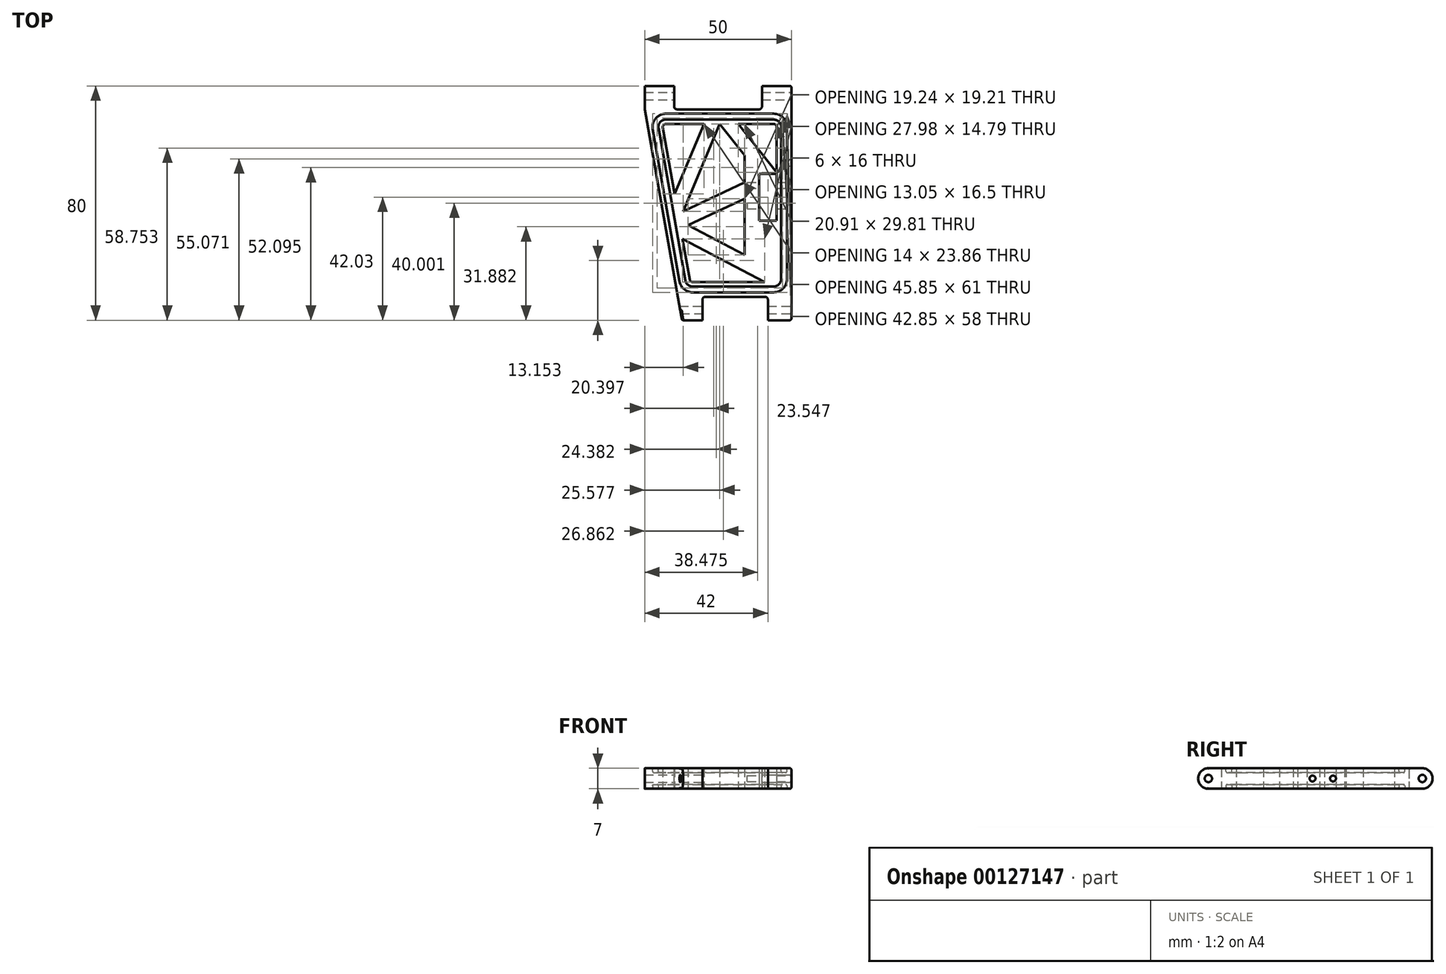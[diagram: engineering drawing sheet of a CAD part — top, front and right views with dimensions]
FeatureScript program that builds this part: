
annotation { "Feature Type Name" : "Feature", "Feature Type Description" : "" }
export const myFeature = defineFeature(function(context is Context, id is Id, definition is map)
    precondition{}
    {
        {
            var Q0;
            Q0=qCreatedBy(makeId("Top.planeOp"),FACE);
            var sketch = newSketch(context, id + "F0", { "sketchPlane" : qUnion([Q0])});
            skLineSegment(sketch, "E0", {"start": v(-39, 45.97) * mm, "end": v(-39, 37.97) * mm});
            skLineSegment(sketch, "E1", {"start": v(-39, 37.97) * mm, "end": v(-26.3, -34.03) * mm});
            skLineSegment(sketch, "E2", {"start": v(11, -34.03) * mm, "end": v(11, 45.97) * mm});
            skLineSegment(sketch, "E3", {"start": v(11, 45.97) * mm, "end": v(1, 45.97) * mm});
            skLineSegment(sketch, "E4", {"start": v(1, 45.97) * mm, "end": v(1, 38.97) * mm});
            skLineSegment(sketch, "E5", {"start": v(-39, 45.97) * mm, "end": v(-29, 45.97) * mm});
            skLineSegment(sketch, "E6", {"start": v(-29, 45.97) * mm, "end": v(-29, 38.97) * mm});
            skLineSegment(sketch, "E7", {"start": v(-28, 37.97) * mm, "end": v(0, 37.97) * mm});
            skLineSegment(sketch, "E8", {"start": v(-26.3, -34.03) * mm, "end": v(-19.3, -34.03) * mm});
            skLineSegment(sketch, "E9", {"start": v(-19.3, -34.03) * mm, "end": v(-19.3, -27.03) * mm});
            skLineSegment(sketch, "E10", {"start": v(11, -34.03) * mm, "end": v(3, -34.03) * mm});
            skLineSegment(sketch, "E11", {"start": v(3, -34.03) * mm, "end": v(3, -27.03) * mm});
            skLineSegment(sketch, "E12", {"start": v(2, -26.03) * mm, "end": v(-18.3, -26.03) * mm});
            skPoint(sketch, "E13.visualSharp", {"position": v(-29, 37.97) * mm});
            skArc(sketch, "E13.filletArc", {"start": v(-29, 38.97) * mm, "mid": v(-28.7, 38.26) * mm, "end": v(-28, 37.97) * mm});
            skPoint(sketch, "E14.visualSharp", {"position": v(1, 37.97) * mm});
            skArc(sketch, "E14.filletArc", {"start": v(0, 37.97) * mm, "mid": v(0.7, 38.26) * mm, "end": v(1, 38.97) * mm});
            skPoint(sketch, "E15.visualSharp", {"position": v(-19.3, -26.03) * mm});
            skArc(sketch, "E15.filletArc", {"start": v(-18.3, -26.03) * mm, "mid": v(-19.01, -26.32) * mm, "end": v(-19.3, -27.03) * mm});
            skPoint(sketch, "E16.visualSharp", {"position": v(3, -26.03) * mm});
            skArc(sketch, "E16.filletArc", {"start": v(3, -27.03) * mm, "mid": v(2.7, -26.32) * mm, "end": v(2, -26.03) * mm});
            skLineSegment(sketch, "E17", {"start": v(6, -20.03) * mm, "end": v(6, 31.97) * mm});
            skLineSegment(sketch, "E18", {"start": v(5, 32.97) * mm, "end": v(-31.85, 32.97) * mm});
            skLineSegment(sketch, "E19", {"start": v(-32.83, 31.8) * mm, "end": v(-23.67, -20.2) * mm});
            skLineSegment(sketch, "E20", {"start": v(-22.68, -21.03) * mm, "end": v(5, -21.03) * mm});
            skPoint(sketch, "E21.visualSharp", {"position": v(-33.04, 32.97) * mm});
            skArc(sketch, "E21.filletArc", {"start": v(-31.85, 32.97) * mm, "mid": v(-32.62, 32.61) * mm, "end": v(-32.83, 31.8) * mm});
            skPoint(sketch, "E22.visualSharp", {"position": v(6, 32.97) * mm});
            skArc(sketch, "E22.filletArc", {"start": v(6, 31.97) * mm, "mid": v(5.7, 32.68) * mm, "end": v(5, 32.97) * mm});
            skPoint(sketch, "E23.visualSharp", {"position": v(-23.52, -21.03) * mm});
            skArc(sketch, "E23.filletArc", {"start": v(-23.67, -20.2) * mm, "mid": v(-23.32, -20.8) * mm, "end": v(-22.68, -21.03) * mm});
            skPoint(sketch, "E24.visualSharp", {"position": v(6, -21.03) * mm});
            skArc(sketch, "E24.filletArc", {"start": v(5, -21.03) * mm, "mid": v(5.7, -20.74) * mm, "end": v(6, -20.03) * mm});
            skLineSegment(sketch, "E25", {"start": v(0, 0) * mm, "end": v(0, 16) * mm});
            skLineSegment(sketch, "E26", {"start": v(0, 16) * mm, "end": v(6, 16) * mm});
            skLineSegment(sketch, "E27", {"start": v(0, 0) * mm, "end": v(6, 0) * mm});
            skLineSegment(sketch, "E28", {"start": v(-13.42, 32.97) * mm, "end": v(0, 16) * mm});
            skLineSegment(sketch, "E29", {"start": v(-7.05, 32.97) * mm, "end": v(6, 16.47) * mm});
            skPoint(sketch, "E29.startSnap0", {"position": v(-6.71, 24.49) * mm});
            skPoint(sketch, "E29.endSnap0", {"position": v(3, 16) * mm});
            skLineSegment(sketch, "E30", {"start": v(-13.42, 32.97) * mm, "end": v(-13.42, -21.03) * mm, "construction": true});
            skLineSegment(sketch, "E31", {"start": v(-13.42, 32.97) * mm, "end": v(-27.23, 0) * mm});
            skLineSegment(sketch, "E32", {"start": v(-18.74, 33.22) * mm, "end": v(-28.83, 9.11) * mm});
            skLineSegment(sketch, "E33", {"start": v(-27.23, 0) * mm, "end": v(6, -17.57) * mm});
            skLineSegment(sketch, "E34", {"start": v(-26.13, -6.24) * mm, "end": v(1.85, -21.03) * mm});
            skLineSegment(sketch, "E35", {"start": v(-5, 22.32) * mm, "end": v(-5, -11.75) * mm});
            skLineSegment(sketch, "E36", {"start": v(-25.9, 3.16) * mm, "end": v(-5, 12.98) * mm});
            skLineSegment(sketch, "E37", {"start": v(-24.24, -1.58) * mm, "end": v(-5, 7.45) * mm});
            skArc(sketch, "E38.0", {"start": v(7.5, 31.97) * mm, "mid": v(6.77, 33.74) * mm, "end": v(5, 34.47) * mm});
            skLineSegment(sketch, "E38.1", {"start": v(7.5, -20.03) * mm, "end": v(7.5, 31.97) * mm});
            skLineSegment(sketch, "E38.2", {"start": v(5, 34.47) * mm, "end": v(-31.85, 34.47) * mm});
            skArc(sketch, "E38.3", {"start": v(5, -22.53) * mm, "mid": v(6.77, -21.8) * mm, "end": v(7.5, -20.03) * mm});
            skArc(sketch, "E38.4", {"start": v(-31.85, 34.47) * mm, "mid": v(-33.76, 33.58) * mm, "end": v(-34.31, 31.54) * mm});
            skLineSegment(sketch, "E38.5", {"start": v(-34.31, 31.54) * mm, "end": v(-25.14, -20.46) * mm});
            skArc(sketch, "E38.6", {"start": v(-25.14, -20.46) * mm, "mid": v(-24.29, -21.94) * mm, "end": v(-22.68, -22.53) * mm});
            skLineSegment(sketch, "E38.7", {"start": v(-22.68, -22.53) * mm, "end": v(5, -22.53) * mm});
            skArc(sketch, "E39.0", {"start": v(9.5, 31.97) * mm, "mid": v(8.18, 35.15) * mm, "end": v(5, 36.47) * mm});
            skLineSegment(sketch, "E39.1", {"start": v(9.5, -20.03) * mm, "end": v(9.5, 31.97) * mm});
            skLineSegment(sketch, "E39.2", {"start": v(5, 36.47) * mm, "end": v(-31.85, 36.47) * mm});
            skArc(sketch, "E39.3", {"start": v(5, -24.53) * mm, "mid": v(8.18, -23.21) * mm, "end": v(9.5, -20.03) * mm});
            skArc(sketch, "E39.4", {"start": v(-31.85, 36.47) * mm, "mid": v(-35.3, 34.86) * mm, "end": v(-36.28, 31.19) * mm});
            skLineSegment(sketch, "E39.5", {"start": v(-36.28, 31.19) * mm, "end": v(-27.11, -20.81) * mm});
            skArc(sketch, "E39.6", {"start": v(-27.11, -20.81) * mm, "mid": v(-25.57, -23.48) * mm, "end": v(-22.68, -24.53) * mm});
            skLineSegment(sketch, "E39.7", {"start": v(-22.68, -24.53) * mm, "end": v(5, -24.53) * mm});
            skSolve(sketch);
        }
        {
            var Q0;
            Q0=makeQuery(id+"F0.imprint","IMPRINT",FACE,{"disambiguationData":[TD([[makeQuery(id+"F0.imprint","IMPRINT",EDGE,{"derivedFrom":sQuery(id+"F0.wireOp",EDGE,"E0")}),1.0]])]});
            var Q1;
            Q1=makeQuery(id+"F0.imprint","IMPRINT",FACE,{"disambiguationData":[TD([[makeQuery(id+"F0.imprint","IMPRINT",EDGE,{"derivedFrom":sQuery(id+"F0.wireOp",EDGE,"E38.0")}),-1.0]])]});
            var Q2;
            {var subQ22=sQuery(id+"F0.wireOp",EDGE,"E21.filletArc");Q2=makeQuery(id+"F0.imprint","IMPRINT",FACE,{"disambiguationData":[TD([[makeQuery(id+"F0.imprint","IMPRINT",EDGE,{"derivedFrom":subQ22}),-1.0]])]});}
            var Q3;
            {var subQ0=sQuery(id+"F0.wireOp",EDGE,"E24.filletArc");Q3=makeQuery(id+"F0.imprint","IMPRINT",FACE,{"disambiguationData":[TD([[makeQuery(id+"F0.imprint","IMPRINT",EDGE,{"derivedFrom":subQ0}),1.0]])]});}
            var Q4;
            {var subQ0=sQuery(id+"F0.wireOp",EDGE,"E36");Q4=makeQuery(id+"F0.imprint","IMPRINT",FACE,{"disambiguationData":[TD([[makeQuery(id+"F0.imprint","IMPRINT",EDGE,{"derivedFrom":subQ0}),-1.0]])]});}
            var Q5;
            {var subQ1=sQuery(id+"F0.wireOp",EDGE,"E19");var subQ6=sQuery(id+"F0.wireOp",EDGE,"E32");var subQ7=makeQuery(id+"F0.imprint","INTERSECT",VERTEX,{"derivedFrom":[subQ1,subQ6]});Q5=makeQuery(id+"F0.imprint","IMPRINT",FACE,{"disambiguationData":[TD([[makeQuery(id+"F0.imprint","IMPRINT",EDGE,{"disambiguationData":[TD([[subQ7,1.0]])],"derivedFrom":subQ6}),1.0]])]});}
            var Q6;
            {var subQ1=sQuery(id+"F0.wireOp",EDGE,"E25");Q6=makeQuery(id+"F0.imprint","IMPRINT",FACE,{"disambiguationData":[TD([[makeQuery(id+"F0.imprint","IMPRINT",EDGE,{"derivedFrom":subQ1}),1.0]])]});}
            var Q7;
            {var subQ5=sQuery(id+"F0.wireOp",EDGE,"E26");Q7=makeQuery(id+"F0.imprint","IMPRINT",FACE,{"disambiguationData":[TD([[makeQuery(id+"F0.imprint","IMPRINT",EDGE,{"derivedFrom":subQ5}),1.0]])]});}
            extrude(context, id + "F1", {"entities" : qUnion([Q0, Q1, Q2, Q3, Q4, Q5, Q6, Q7]), "endBound" : BoundingType.SYMMETRIC, "depth" : 7 * mm});
        }
        {
            var Q0;
            Q0=qCreatedBy(makeId("Right.planeOp"),FACE);
            var sketch = newSketch(context, id + "F2", { "sketchPlane" : qUnion([Q0])});
            skLineSegment(sketch, "E40.0", {"start": v(45.97, 3.5) * mm, "end": v(45.97, -3.5) * mm});
            skLineSegment(sketch, "E40.1", {"start": v(-34.03, 3.5) * mm, "end": v(45.97, 3.5) * mm});
            skLineSegment(sketch, "E40.2", {"start": v(-34.03, -3.5) * mm, "end": v(45.97, -3.5) * mm});
            skLineSegment(sketch, "E40.3", {"start": v(-34.03, 3.5) * mm, "end": v(-34.03, -3.5) * mm});
            skCircle(sketch, "E41", {"center": v(42.47, 0) * mm, "radius": 3.5 * mm});
            skCircle(sketch, "E42", {"center": v(42.47, 0) * mm, "radius": 1.25 * mm});
            skCircle(sketch, "E43", {"center": v(-30.53, 0) * mm, "radius": 3.5 * mm});
            skCircle(sketch, "E44", {"center": v(-30.53, 0) * mm, "radius": 1.25 * mm});
            skSolve(sketch);
        }
        {
            var Q0;
            Q0=makeQuery(id+"F1.opExtrude","SWEPT_FACE",FACE,{"disambiguationData":[OSD([sQuery(id+"F0.wireOp",EDGE,"E2")])]});
            var sketch = newSketch(context, id + "F3", { "sketchPlane" : qUnion([Q0])});
            skCircle(sketch, "E45.0", {"center": v(42.47, 0) * mm, "radius": 3.5 * mm});
            skCircle(sketch, "E45.1", {"center": v(42.47, 0) * mm, "radius": 1.25 * mm});
            skCircle(sketch, "E45.2", {"center": v(-30.53, 0) * mm, "radius": 1.25 * mm});
            skCircle(sketch, "E45.3", {"center": v(-30.53, 0) * mm, "radius": 3.5 * mm});
            skCircle(sketch, "E46", {"center": v(5, 0) * mm, "radius": 1 * mm});
            skCircle(sketch, "E47", {"center": v(12, 0) * mm, "radius": 1 * mm});
            skLineSegment(sketch, "E48", {"start": v(5, 3.5) * mm, "end": v(5, -3.5) * mm, "construction": true});
            skLineSegment(sketch, "E49", {"start": v(12, 3.5) * mm, "end": v(12, -3.5) * mm, "construction": true});
            skSolve(sketch);
        }
        {
            var Q0;
            {var subQ0=sQuery(id+"F3.wireOp",EDGE,"E45.3");var subQ1=sQuery(id+"F0.wireOp",EDGE,"E2");var subQ2=makeQuery(id+"F1.opExtrude","CAP_EDGE",EDGE,{"disambiguationData":[OSD([subQ1])],"isStart":false});var subQ3=makeQuery(id+"F3.imprint","INTERSECT",VERTEX,{"derivedFrom":[subQ2,subQ0]});Q0=makeQuery(id+"F3.imprint","IMPRINT",FACE,{"disambiguationData":[TD([[makeQuery(id+"F3.imprint","IMPRINT",EDGE,{"disambiguationData":[TD([[subQ3,-1.0]])],"derivedFrom":subQ0}),-1.0]])]});}
            var Q1;
            {var subQ0=sQuery(id+"F3.wireOp",EDGE,"E45.3");var subQ1=sQuery(id+"F0.wireOp",EDGE,"E2");var subQ2=makeQuery(id+"F1.opExtrude","CAP_EDGE",EDGE,{"disambiguationData":[OSD([subQ1])],"isStart":true});var subQ3=makeQuery(id+"F3.imprint","INTERSECT",VERTEX,{"derivedFrom":[subQ2,subQ0]});Q1=makeQuery(id+"F3.imprint","IMPRINT",FACE,{"disambiguationData":[TD([[makeQuery(id+"F3.imprint","IMPRINT",EDGE,{"disambiguationData":[TD([[subQ3,1.0]])],"derivedFrom":subQ0}),-1.0]])]});}
            var Q2;
            {var subQ0=sQuery(id+"F3.wireOp",EDGE,"E45.0");var subQ1=sQuery(id+"F0.wireOp",EDGE,"E2");var subQ4=makeQuery(id+"F1.opExtrude","CAP_EDGE",EDGE,{"disambiguationData":[OSD([subQ1])],"isStart":false});var subQ5=makeQuery(id+"F3.imprint","INTERSECT",VERTEX,{"derivedFrom":[subQ4,subQ0]});Q2=makeQuery(id+"F3.imprint","IMPRINT",FACE,{"disambiguationData":[TD([[makeQuery(id+"F3.imprint","IMPRINT",EDGE,{"disambiguationData":[TD([[subQ5,1.0]])],"derivedFrom":subQ0}),-1.0]])]});}
            var Q3;
            {var subQ0=sQuery(id+"F3.wireOp",EDGE,"E45.0");var subQ1=sQuery(id+"F0.wireOp",EDGE,"E2");var subQ4=makeQuery(id+"F1.opExtrude","CAP_EDGE",EDGE,{"disambiguationData":[OSD([subQ1])],"isStart":true});var subQ5=makeQuery(id+"F3.imprint","INTERSECT",VERTEX,{"derivedFrom":[subQ4,subQ0]});Q3=makeQuery(id+"F3.imprint","IMPRINT",FACE,{"disambiguationData":[TD([[makeQuery(id+"F3.imprint","IMPRINT",EDGE,{"disambiguationData":[TD([[subQ5,-1.0]])],"derivedFrom":subQ0}),-1.0]])]});}
            var Q4;
            Q4=makeQuery(id+"F3.imprint","IMPRINT",FACE,{"disambiguationData":[TD([[makeQuery(id+"F3.imprint","IMPRINT",EDGE,{"derivedFrom":sQuery(id+"F3.wireOp",EDGE,"E45.1")}),1.0]])]});
            var Q5;
            Q5=makeQuery(id+"F3.imprint","IMPRINT",FACE,{"disambiguationData":[TD([[makeQuery(id+"F3.imprint","IMPRINT",EDGE,{"derivedFrom":sQuery(id+"F3.wireOp",EDGE,"E45.2")}),1.0]])]});
            extrude(context, id + "F4", {"entities" : qUnion([Q0, Q1, Q2, Q3, Q4, Q5]), "operationType" : NewBodyOperationType.REMOVE, "endBound" : BoundingType.THROUGH_ALL, "oppositeDirection" : true, "depth" : 25 * mm});
        }
        {
            var Q0;
            Q0=makeQuery(id+"F3.imprint","IMPRINT",FACE,{"disambiguationData":[TD([[makeQuery(id+"F3.imprint","IMPRINT",EDGE,{"derivedFrom":sQuery(id+"F3.wireOp",EDGE,"E46")}),1.0]])]});
            var Q1;
            Q1=makeQuery(id+"F3.imprint","IMPRINT",FACE,{"disambiguationData":[TD([[makeQuery(id+"F3.imprint","IMPRINT",EDGE,{"derivedFrom":sQuery(id+"F3.wireOp",EDGE,"E47")}),1.0]])]});
            extrude(context, id + "F5", {"entities" : qUnion([Q0, Q1]), "operationType" : NewBodyOperationType.REMOVE, "oppositeDirection" : true, "depth" : 15 * mm});
        }
        {
            var Q0;
            Q0=makeQuery(id+"F1.opExtrude","CAP_FACE",FACE,{"disambiguationData":[OSD([sQuery(id+"F0.wireOp",EDGE,"E0"),sQuery(id+"F0.wireOp",EDGE,"E1"),sQuery(id+"F0.wireOp",EDGE,"E2"),sQuery(id+"F0.wireOp",EDGE,"E3"),sQuery(id+"F0.wireOp",EDGE,"E4"),sQuery(id+"F0.wireOp",EDGE,"E5"),sQuery(id+"F0.wireOp",EDGE,"E6"),sQuery(id+"F0.wireOp",EDGE,"E7"),sQuery(id+"F0.wireOp",EDGE,"E8"),sQuery(id+"F0.wireOp",EDGE,"E9"),sQuery(id+"F0.wireOp",EDGE,"E10"),sQuery(id+"F0.wireOp",EDGE,"E11"),sQuery(id+"F0.wireOp",EDGE,"E12"),sQuery(id+"F0.wireOp",EDGE,"E13.filletArc"),sQuery(id+"F0.wireOp",EDGE,"E14.filletArc"),sQuery(id+"F0.wireOp",EDGE,"E15.filletArc"),sQuery(id+"F0.wireOp",EDGE,"E16.filletArc"),sQuery(id+"F0.wireOp",EDGE,"E17"),sQuery(id+"F0.wireOp",EDGE,"E18"),sQuery(id+"F0.wireOp",EDGE,"E19"),sQuery(id+"F0.wireOp",EDGE,"E20"),sQuery(id+"F0.wireOp",EDGE,"E21.filletArc"),sQuery(id+"F0.wireOp",EDGE,"E22.filletArc"),sQuery(id+"F0.wireOp",EDGE,"E23.filletArc"),sQuery(id+"F0.wireOp",EDGE,"E25"),sQuery(id+"F0.wireOp",EDGE,"E26"),sQuery(id+"F0.wireOp",EDGE,"E27"),sQuery(id+"F0.wireOp",EDGE,"E28"),sQuery(id+"F0.wireOp",EDGE,"E29"),sQuery(id+"F0.wireOp",EDGE,"E31"),sQuery(id+"F0.wireOp",EDGE,"E32"),sQuery(id+"F0.wireOp",EDGE,"E33"),sQuery(id+"F0.wireOp",EDGE,"E34"),sQuery(id+"F0.wireOp",EDGE,"E35"),sQuery(id+"F0.wireOp",EDGE,"E36"),sQuery(id+"F0.wireOp",EDGE,"E37")])],"isStart":false});
            var sketch = newSketch(context, id + "F6", { "sketchPlane" : qUnion([Q0])});
            skArc(sketch, "E50.0", {"start": v(-31.85, 36.47) * mm, "mid": v(-35.3, 34.86) * mm, "end": v(-36.28, 31.19) * mm});
            skLineSegment(sketch, "E50.1", {"start": v(5, 36.47) * mm, "end": v(-31.85, 36.47) * mm});
            skArc(sketch, "E50.2", {"start": v(9.5, 31.97) * mm, "mid": v(8.18, 35.15) * mm, "end": v(5, 36.47) * mm});
            skLineSegment(sketch, "E50.3", {"start": v(5, 34.47) * mm, "end": v(-31.85, 34.47) * mm});
            skArc(sketch, "E50.4", {"start": v(7.5, 31.97) * mm, "mid": v(6.77, 33.74) * mm, "end": v(5, 34.47) * mm});
            skArc(sketch, "E50.5", {"start": v(-31.85, 34.47) * mm, "mid": v(-33.76, 33.58) * mm, "end": v(-34.31, 31.54) * mm});
            skLineSegment(sketch, "E50.6", {"start": v(-36.28, 31.19) * mm, "end": v(-27.11, -20.81) * mm});
            skLineSegment(sketch, "E50.7", {"start": v(-34.31, 31.54) * mm, "end": v(-25.14, -20.46) * mm});
            skLineSegment(sketch, "E50.8", {"start": v(7.5, -20.03) * mm, "end": v(7.5, 31.97) * mm});
            skLineSegment(sketch, "E50.9", {"start": v(9.5, -20.03) * mm, "end": v(9.5, 31.97) * mm});
            skArc(sketch, "E50.10", {"start": v(-27.11, -20.81) * mm, "mid": v(-25.57, -23.48) * mm, "end": v(-22.68, -24.53) * mm});
            skArc(sketch, "E50.11", {"start": v(-25.14, -20.46) * mm, "mid": v(-24.29, -21.94) * mm, "end": v(-22.68, -22.53) * mm});
            skLineSegment(sketch, "E50.12", {"start": v(-22.68, -22.53) * mm, "end": v(5, -22.53) * mm});
            skLineSegment(sketch, "E50.13", {"start": v(-22.68, -24.53) * mm, "end": v(5, -24.53) * mm});
            skArc(sketch, "E50.14", {"start": v(5, -24.53) * mm, "mid": v(8.18, -23.21) * mm, "end": v(9.5, -20.03) * mm});
            skArc(sketch, "E50.15", {"start": v(5, -22.53) * mm, "mid": v(6.77, -21.8) * mm, "end": v(7.5, -20.03) * mm});
            skSolve(sketch);
        }
        {
            var Q0;
            Q0 = qSketchRegion(id + "F6", true);
            extrude(context, id + "F7", {"entities" : qUnion([Q0]), "operationType" : NewBodyOperationType.REMOVE, "oppositeDirection" : true, "depth" : 1.5 * mm});
        }
        {
            var Q0;
            Q0=makeQuery(id+"F7.boolean.opBoolean","COPY",EDGE,{"derivedFrom":makeQuery(id+"F7.opExtrude","CAP_EDGE",EDGE,{"disambiguationData":[OSD([sQuery(id+"F6.wireOp",EDGE,"E50.6")])],"isStart":true})});
            var Q1;
            Q1=makeQuery(id+"F7.boolean.opBoolean","COPY",EDGE,{"derivedFrom":makeQuery(id+"F7.opExtrude","CAP_EDGE",EDGE,{"disambiguationData":[OSD([sQuery(id+"F6.wireOp",EDGE,"E50.7")])],"isStart":true})});
            fillet(context, id + "F8", {"entities" : qUnion([Q0, Q1]), "radius" : .5 * mm, "tangentPropagation" : true, "allowEdgeOverflow" : false});
        }
        {
            var Q0;
            Q0=makeQuery(id+"F7.boolean.opBoolean","COPY",FACE,{"derivedFrom":makeQuery(id+"F7.opExtrude","CAP_FACE",FACE,{"disambiguationData":[OSD([sQuery(id+"F6.wireOp",EDGE,"E50.0"),sQuery(id+"F6.wireOp",EDGE,"E50.1"),sQuery(id+"F6.wireOp",EDGE,"E50.2"),sQuery(id+"F6.wireOp",EDGE,"E50.3"),sQuery(id+"F6.wireOp",EDGE,"E50.4"),sQuery(id+"F6.wireOp",EDGE,"E50.5"),sQuery(id+"F6.wireOp",EDGE,"E50.6"),sQuery(id+"F6.wireOp",EDGE,"E50.7"),sQuery(id+"F6.wireOp",EDGE,"E50.8"),sQuery(id+"F6.wireOp",EDGE,"E50.9"),sQuery(id+"F6.wireOp",EDGE,"E50.10"),sQuery(id+"F6.wireOp",EDGE,"E50.11"),sQuery(id+"F6.wireOp",EDGE,"E50.12"),sQuery(id+"F6.wireOp",EDGE,"E50.13"),sQuery(id+"F6.wireOp",EDGE,"E50.14"),sQuery(id+"F6.wireOp",EDGE,"E50.15")])],"isStart":false})});
            fillet(context, id + "F9", {"entities" : qUnion([Q0]), "radius" : .5 * mm, "tangentPropagation" : true, "allowEdgeOverflow" : false});
        }
        {
            var Q0;
            Q0=makeQuery(id+"F1.opExtrude","CAP_EDGE",EDGE,{"disambiguationData":[OSD([sQuery(id+"F0.wireOp",EDGE,"E1")])],"isStart":false});
            fillet(context, id + "F10", {"entities" : qUnion([Q0]), "radius" : .5 * mm, "tangentPropagation" : true, "allowEdgeOverflow" : false});
        }
        {
            var Q0;
            Q0=makeQuery(id+"F1.opExtrude","CAP_EDGE",EDGE,{"disambiguationData":[OSD([sQuery(id+"F0.wireOp",EDGE,"E2")])],"isStart":false});
            var Q1;
            {var subQ0=sQuery(id+"F3.wireOp",EDGE,"E45.0");var subQ1=sQuery(id+"F0.wireOp",EDGE,"E2");Q1=makeQuery(id+"F4.boolean.opBoolean","TWEAK_EDGE",EDGE,{"derivedFrom":[makeQuery(id+"F4.opExtrude","CAP_EDGE",EDGE,{"disambiguationData":[OSD([subQ0]),TDD([makeQuery(id+"F3.imprint","IMPRINT",EDGE,{"disambiguationData":[TD([[makeQuery(id+"F3.imprint","INTERSECT",VERTEX,{"derivedFrom":[makeQuery(id+"F1.opExtrude","CAP_EDGE",EDGE,{"disambiguationData":[OSD([subQ1])],"isStart":true}),subQ0]}),-1.0]])],"derivedFrom":subQ0})])],"isStart":true}),makeQuery(id+"F4.opExtrude","CAP_EDGE",EDGE,{"disambiguationData":[OSD([subQ0]),TDD([makeQuery(id+"F3.imprint","IMPRINT",EDGE,{"disambiguationData":[TD([[makeQuery(id+"F3.imprint","INTERSECT",VERTEX,{"derivedFrom":[makeQuery(id+"F1.opExtrude","CAP_EDGE",EDGE,{"disambiguationData":[OSD([subQ1])],"isStart":false}),subQ0]}),1.0]])],"derivedFrom":subQ0})])],"isStart":true})]});}
            fillet(context, id + "F11", {"entities" : qUnion([Q0, Q1]), "radius" : .5 * mm, "tangentPropagation" : true, "allowEdgeOverflow" : false});
        }
        {
            var Q0;
            Q0=makeQuery(id+"F1.opExtrude","CAP_FACE",FACE,{"disambiguationData":[OSD([sQuery(id+"F0.wireOp",EDGE,"E0"),sQuery(id+"F0.wireOp",EDGE,"E1"),sQuery(id+"F0.wireOp",EDGE,"E2"),sQuery(id+"F0.wireOp",EDGE,"E3"),sQuery(id+"F0.wireOp",EDGE,"E4"),sQuery(id+"F0.wireOp",EDGE,"E5"),sQuery(id+"F0.wireOp",EDGE,"E6"),sQuery(id+"F0.wireOp",EDGE,"E7"),sQuery(id+"F0.wireOp",EDGE,"E8"),sQuery(id+"F0.wireOp",EDGE,"E9"),sQuery(id+"F0.wireOp",EDGE,"E10"),sQuery(id+"F0.wireOp",EDGE,"E11"),sQuery(id+"F0.wireOp",EDGE,"E12"),sQuery(id+"F0.wireOp",EDGE,"E13.filletArc"),sQuery(id+"F0.wireOp",EDGE,"E14.filletArc"),sQuery(id+"F0.wireOp",EDGE,"E15.filletArc"),sQuery(id+"F0.wireOp",EDGE,"E16.filletArc"),sQuery(id+"F0.wireOp",EDGE,"E17"),sQuery(id+"F0.wireOp",EDGE,"E18"),sQuery(id+"F0.wireOp",EDGE,"E19"),sQuery(id+"F0.wireOp",EDGE,"E20"),sQuery(id+"F0.wireOp",EDGE,"E21.filletArc"),sQuery(id+"F0.wireOp",EDGE,"E22.filletArc"),sQuery(id+"F0.wireOp",EDGE,"E23.filletArc"),sQuery(id+"F0.wireOp",EDGE,"E25"),sQuery(id+"F0.wireOp",EDGE,"E26"),sQuery(id+"F0.wireOp",EDGE,"E27"),sQuery(id+"F0.wireOp",EDGE,"E28"),sQuery(id+"F0.wireOp",EDGE,"E29"),sQuery(id+"F0.wireOp",EDGE,"E31"),sQuery(id+"F0.wireOp",EDGE,"E32"),sQuery(id+"F0.wireOp",EDGE,"E33"),sQuery(id+"F0.wireOp",EDGE,"E34"),sQuery(id+"F0.wireOp",EDGE,"E35"),sQuery(id+"F0.wireOp",EDGE,"E36"),sQuery(id+"F0.wireOp",EDGE,"E37")])],"isStart":true});
            var sketch = newSketch(context, id + "F12", { "sketchPlane" : qUnion([Q0])});
            skArc(sketch, "E51.0", {"start": v(-31.85, -36.47) * mm, "mid": v(-35.3, -34.86) * mm, "end": v(-36.28, -31.19) * mm});
            skLineSegment(sketch, "E51.1", {"start": v(5, -36.47) * mm, "end": v(-31.85, -36.47) * mm});
            skLineSegment(sketch, "E51.2", {"start": v(5, -34.47) * mm, "end": v(-31.85, -34.47) * mm});
            skArc(sketch, "E51.3", {"start": v(-31.85, -34.47) * mm, "mid": v(-33.76, -33.58) * mm, "end": v(-34.31, -31.54) * mm});
            skLineSegment(sketch, "E51.4", {"start": v(-36.28, -31.19) * mm, "end": v(-27.11, 20.81) * mm});
            skLineSegment(sketch, "E51.5", {"start": v(-34.31, -31.54) * mm, "end": v(-25.14, 20.46) * mm});
            skArc(sketch, "E51.6", {"start": v(-25.14, 20.46) * mm, "mid": v(-24.29, 21.94) * mm, "end": v(-22.68, 22.53) * mm});
            skArc(sketch, "E51.7", {"start": v(-27.11, 20.81) * mm, "mid": v(-25.57, 23.48) * mm, "end": v(-22.68, 24.53) * mm});
            skLineSegment(sketch, "E51.8", {"start": v(-22.68, 22.53) * mm, "end": v(5, 22.53) * mm});
            skLineSegment(sketch, "E51.9", {"start": v(-22.68, 24.53) * mm, "end": v(5, 24.53) * mm});
            skArc(sketch, "E51.10", {"start": v(5, 22.53) * mm, "mid": v(6.77, 21.8) * mm, "end": v(7.5, 20.03) * mm});
            skArc(sketch, "E51.11", {"start": v(5, 24.53) * mm, "mid": v(8.18, 23.21) * mm, "end": v(9.5, 20.03) * mm});
            skLineSegment(sketch, "E51.12", {"start": v(9.5, 20.03) * mm, "end": v(9.5, -31.97) * mm});
            skLineSegment(sketch, "E51.13", {"start": v(7.5, 20.03) * mm, "end": v(7.5, -31.97) * mm});
            skArc(sketch, "E51.14", {"start": v(9.5, -31.97) * mm, "mid": v(8.18, -35.15) * mm, "end": v(5, -36.47) * mm});
            skArc(sketch, "E51.15", {"start": v(7.5, -31.97) * mm, "mid": v(6.77, -33.74) * mm, "end": v(5, -34.47) * mm});
            skSolve(sketch);
        }
        {
            var Q0;
            Q0 = qSketchRegion(id + "F12", true);
            extrude(context, id + "F13", {"entities" : qUnion([Q0]), "operationType" : NewBodyOperationType.REMOVE, "oppositeDirection" : true, "depth" : 1.5 * mm});
        }
        {
            var Q0;
            Q0=makeQuery(id+"F13.boolean.opBoolean","COPY",EDGE,{"derivedFrom":makeQuery(id+"F13.opExtrude","CAP_EDGE",EDGE,{"disambiguationData":[OSD([sQuery(id+"F12.wireOp",EDGE,"E51.4")])],"isStart":true})});
            var Q1;
            Q1=makeQuery(id+"F13.boolean.opBoolean","COPY",EDGE,{"derivedFrom":makeQuery(id+"F13.opExtrude","CAP_EDGE",EDGE,{"disambiguationData":[OSD([sQuery(id+"F12.wireOp",EDGE,"E51.5")])],"isStart":true})});
            fillet(context, id + "F14", {"entities" : qUnion([Q0, Q1]), "radius" : .5 * mm, "tangentPropagation" : true, "allowEdgeOverflow" : false});
        }
        {
            var Q0;
            Q0=makeQuery(id+"F13.boolean.opBoolean","COPY",FACE,{"derivedFrom":makeQuery(id+"F13.opExtrude","CAP_FACE",FACE,{"disambiguationData":[OSD([sQuery(id+"F12.wireOp",EDGE,"E51.0"),sQuery(id+"F12.wireOp",EDGE,"E51.1"),sQuery(id+"F12.wireOp",EDGE,"E51.2"),sQuery(id+"F12.wireOp",EDGE,"E51.3"),sQuery(id+"F12.wireOp",EDGE,"E51.4"),sQuery(id+"F12.wireOp",EDGE,"E51.5"),sQuery(id+"F12.wireOp",EDGE,"E51.6"),sQuery(id+"F12.wireOp",EDGE,"E51.7"),sQuery(id+"F12.wireOp",EDGE,"E51.8"),sQuery(id+"F12.wireOp",EDGE,"E51.9"),sQuery(id+"F12.wireOp",EDGE,"E51.10"),sQuery(id+"F12.wireOp",EDGE,"E51.11"),sQuery(id+"F12.wireOp",EDGE,"E51.12"),sQuery(id+"F12.wireOp",EDGE,"E51.13"),sQuery(id+"F12.wireOp",EDGE,"E51.14"),sQuery(id+"F12.wireOp",EDGE,"E51.15")])],"isStart":false})});
            fillet(context, id + "F15", {"entities" : qUnion([Q0]), "radius" : .5 * mm, "tangentPropagation" : true, "allowEdgeOverflow" : false});
        }
    });
